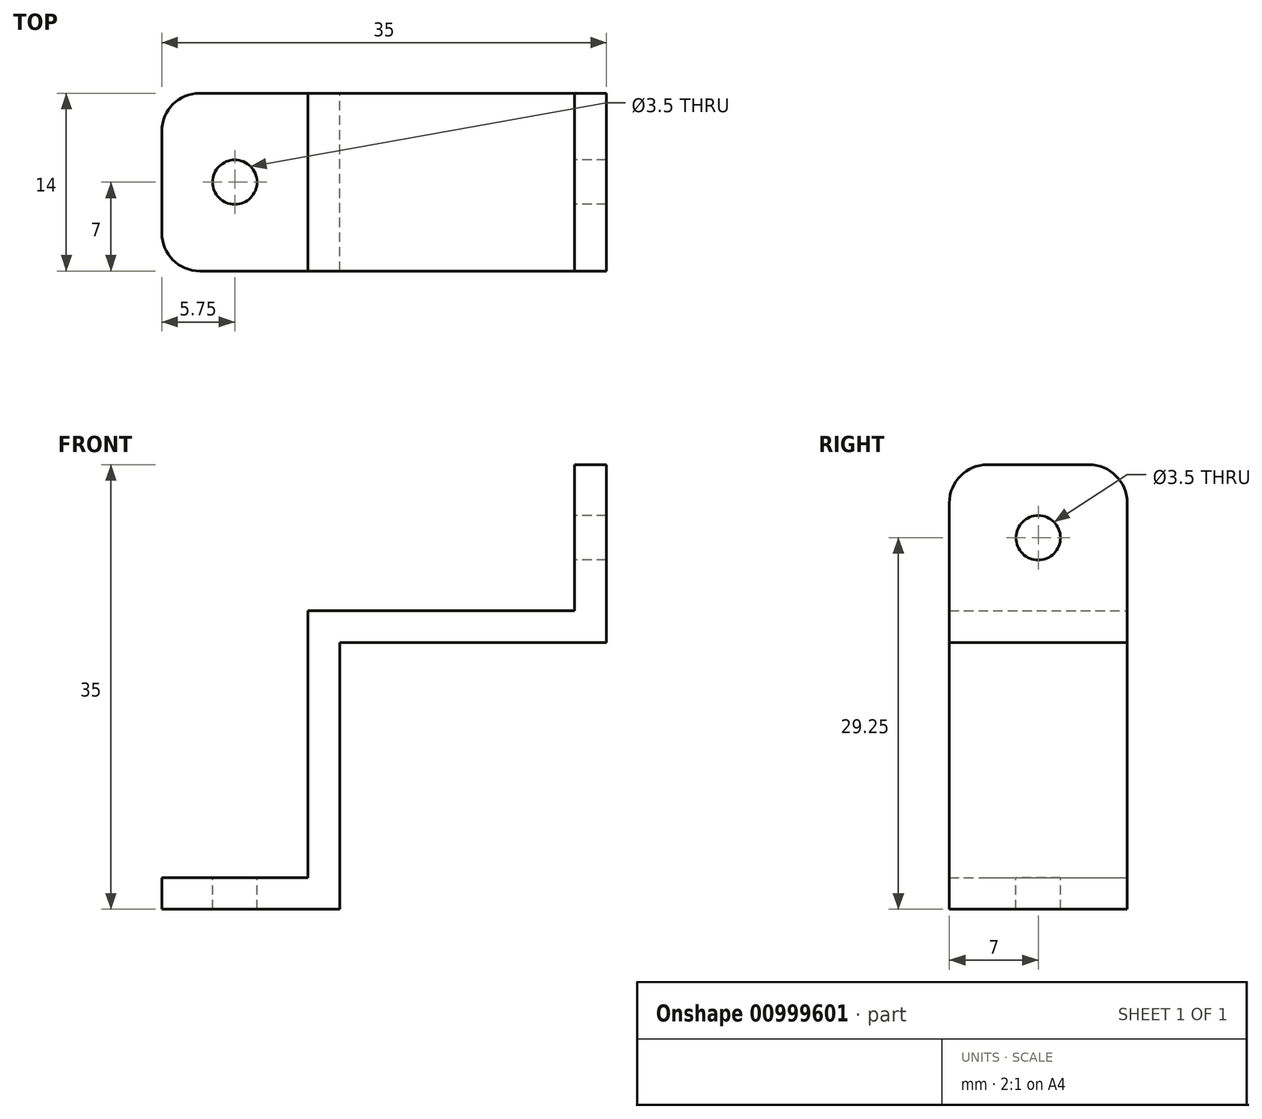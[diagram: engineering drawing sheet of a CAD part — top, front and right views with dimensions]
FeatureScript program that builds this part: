
annotation { "Feature Type Name" : "Feature", "Feature Type Description" : "" }
export const myFeature = defineFeature(function(context is Context, id is Id, definition is map)
    precondition{}
    {
        {
            var Q0;
            Q0=qCreatedBy(makeId("Front.planeOp"),FACE);
            var sketch = newSketch(context, id + "F0", { "sketchPlane" : qUnion([Q0])});
            skLineSegment(sketch, "E0", {"start": v(0, 0) * mm, "end": v(0, 21) * mm});
            skLineSegment(sketch, "E1", {"start": v(0, 21) * mm, "end": v(21, 21) * mm});
            skLineSegment(sketch, "E2", {"start": v(21, 21) * mm, "end": v(21, 35) * mm});
            skLineSegment(sketch, "E3", {"start": v(21, 35) * mm, "end": v(18.5, 35) * mm});
            skLineSegment(sketch, "E4", {"start": v(18.5, 35) * mm, "end": v(18.5, 23.5) * mm});
            skLineSegment(sketch, "E5", {"start": v(18.5, 23.5) * mm, "end": v(-2.5, 23.5) * mm});
            skLineSegment(sketch, "E6", {"start": v(-2.5, 23.5) * mm, "end": v(-2.5, 2.5) * mm});
            skLineSegment(sketch, "E7", {"start": v(-2.5, 2.5) * mm, "end": v(-14, 2.5) * mm});
            skLineSegment(sketch, "E8", {"start": v(-14, 2.5) * mm, "end": v(-14, 0) * mm});
            skLineSegment(sketch, "E9", {"start": v(-14, 0) * mm, "end": v(0, 0) * mm});
            skSolve(sketch);
        }
        {
            var Q0;
            Q0 = qSketchRegion(id + "F0", true);
            extrude(context, id + "F1", {"entities" : qUnion([Q0]), "depth" : 14 * mm, "offsetDistance" : 25 * mm});
        }
        {
            var Q0;
            Q0=makeQuery(id+"F1.opExtrude","SWEPT_FACE",FACE,{"disambiguationData":[OSD([sQuery(id+"F0.wireOp",EDGE,"E4")])]});
            var sketch = newSketch(context, id + "F2", { "sketchPlane" : qUnion([Q0])});
            skCircle(sketch, "E10", {"center": v(7, 29.25) * mm, "radius": 1.75 * mm});
            skPoint(sketch, "E10.centerSnap0", {"position": v(7, 35) * mm});
            skPoint(sketch, "E10.centerSnap1", {"position": v(0, 29.25) * mm});
            skSolve(sketch);
        }
        {
            var Q0;
            Q0 = qSketchRegion(id + "F2", true);
            extrude(context, id + "F3", {"entities" : qUnion([Q0]), "operationType" : NewBodyOperationType.REMOVE, "endBound" : BoundingType.THROUGH_ALL, "oppositeDirection" : true, "depth" : 25 * mm, "offsetDistance" : 25 * mm});
        }
        {
            var Q0;
            Q0=makeQuery(id+"F1.opExtrude","SWEPT_FACE",FACE,{"disambiguationData":[OSD([sQuery(id+"F0.wireOp",EDGE,"E7")])]});
            var sketch = newSketch(context, id + "F4", { "sketchPlane" : qUnion([Q0])});
            skCircle(sketch, "E11", {"center": v(-8.25, -7) * mm, "radius": 1.75 * mm});
            skPoint(sketch, "E11.centerSnap0", {"position": v(-14, -7) * mm});
            skPoint(sketch, "E11.centerSnap1", {"position": v(-8.25, 0) * mm});
            skSolve(sketch);
        }
        {
            var Q0;
            Q0 = qSketchRegion(id + "F4", true);
            extrude(context, id + "F5", {"entities" : qUnion([Q0]), "operationType" : NewBodyOperationType.REMOVE, "oppositeDirection" : true, "depth" : 25 * mm, "offsetDistance" : 25 * mm});
        }
        {
            var Q0;
            Q0=makeQuery(id+"F1.opExtrude","CAP_EDGE",EDGE,{"disambiguationData":[OSD([sQuery(id+"F0.wireOp",EDGE,"E8")])],"isStart":false});
            var Q1;
            Q1=makeQuery(id+"F1.opExtrude","CAP_EDGE",EDGE,{"disambiguationData":[OSD([sQuery(id+"F0.wireOp",EDGE,"E8")])],"isStart":true});
            var Q2;
            Q2=makeQuery(id+"F1.opExtrude","CAP_EDGE",EDGE,{"disambiguationData":[OSD([sQuery(id+"F0.wireOp",EDGE,"E3")])],"isStart":false});
            var Q3;
            Q3=makeQuery(id+"F1.opExtrude","CAP_EDGE",EDGE,{"disambiguationData":[OSD([sQuery(id+"F0.wireOp",EDGE,"E3")])],"isStart":true});
            fillet(context, id + "F6", {"entities" : qUnion([Q0, Q1, Q2, Q3]), "radius" : 3 * mm, "tangentPropagation" : true, "allowEdgeOverflow" : false});
        }
    });
